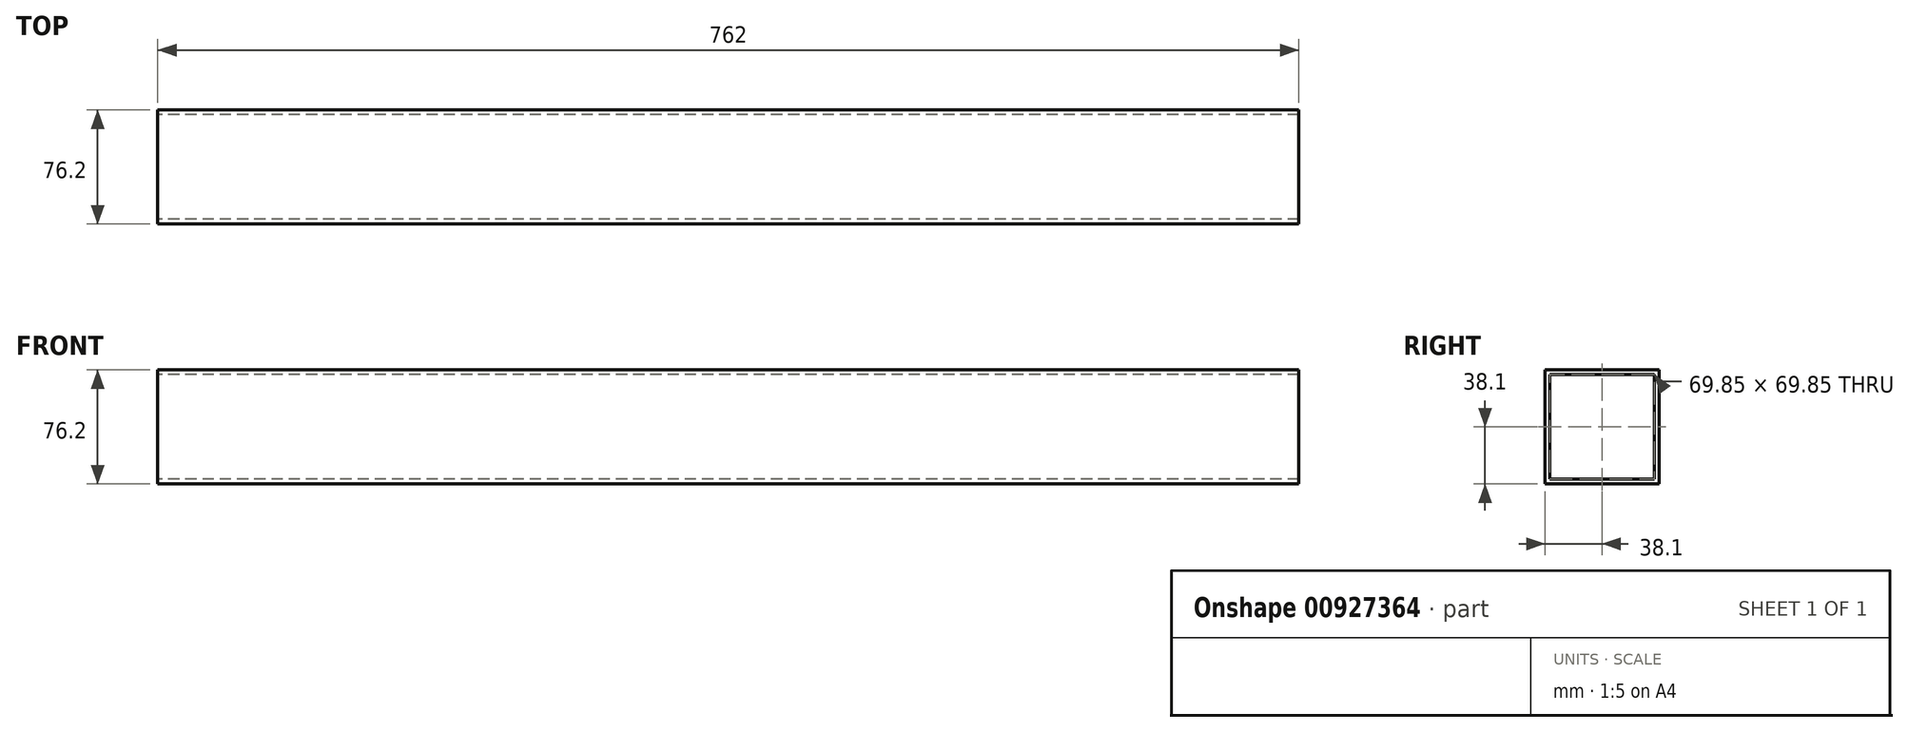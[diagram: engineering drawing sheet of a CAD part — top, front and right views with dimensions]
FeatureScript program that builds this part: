
annotation { "Feature Type Name" : "Feature", "Feature Type Description" : "" }
export const myFeature = defineFeature(function(context is Context, id is Id, definition is map)
    precondition{}
    {
        {
            var Q0;
            Q0=qCreatedBy(makeId("Right.planeOp"),FACE);
            var sketch = newSketch(context, id + "F0", { "sketchPlane" : qUnion([Q0])});
            skLineSegment(sketch, "E0.bottom", {"start": v(-38.1, 38.1) * mm, "end": v(38.1, 38.1) * mm});
            skLineSegment(sketch, "E0.top", {"start": v(-38.1, -38.1) * mm, "end": v(38.1, -38.1) * mm});
            skLineSegment(sketch, "E0.left", {"start": v(-38.1, 38.1) * mm, "end": v(-38.1, -38.1) * mm});
            skLineSegment(sketch, "E0.right", {"start": v(38.1, 38.1) * mm, "end": v(38.1, -38.1) * mm});
            skLineSegment(sketch, "E1.bottom", {"start": v(34.93, 34.92) * mm, "end": v(-34.93, 34.92) * mm});
            skLineSegment(sketch, "E1.top", {"start": v(34.93, -34.92) * mm, "end": v(-34.93, -34.92) * mm});
            skLineSegment(sketch, "E1.left", {"start": v(34.92, 34.92) * mm, "end": v(34.93, -34.93) * mm});
            skLineSegment(sketch, "E1.right", {"start": v(-34.93, 34.92) * mm, "end": v(-34.92, -34.93) * mm});
            skPoint(sketch, "E1.middle", {"position": v(0, 0) * mm});
            skSolve(sketch);
        }
        {
            var Q0;
            Q0=makeQuery(id+"F0.imprint","IMPRINT",FACE,{"disambiguationData":[TD([[makeQuery(id+"F0.imprint","IMPRINT",EDGE,{"derivedFrom":sQuery(id+"F0.wireOp",EDGE,"E0.bottom")}),-1.0]])]});
            extrude(context, id + "F1", {"entities" : qUnion([Q0]), "depth" : 381 * mm, "offsetDistance" : 25.4 * mm, "hasSecondDirection" : true, "secondDirectionOppositeDirection" : true, "secondDirectionDepth" : 381 * mm});
        }
    });
